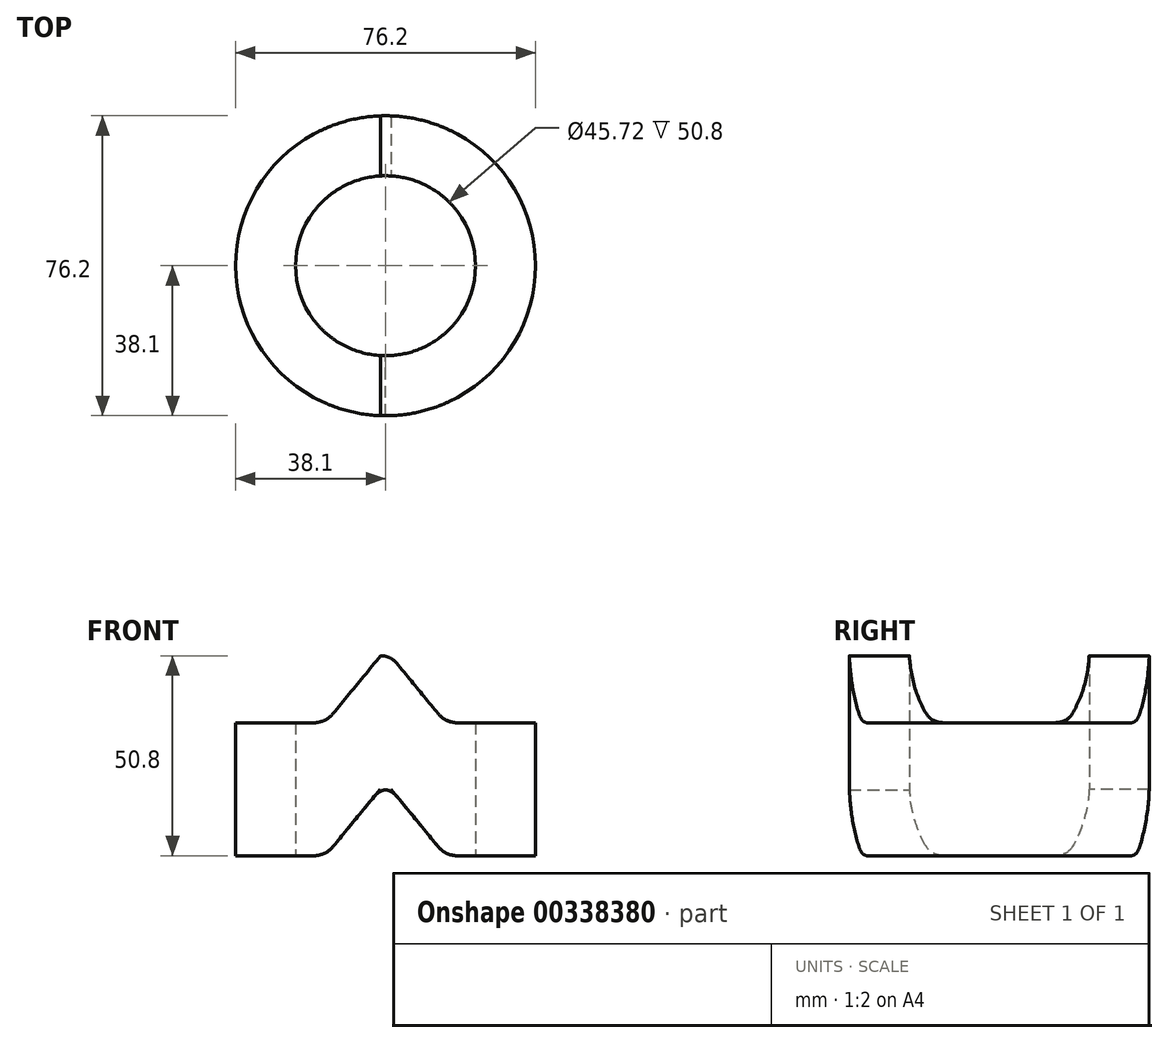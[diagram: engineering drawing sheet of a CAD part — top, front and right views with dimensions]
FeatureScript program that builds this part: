
annotation { "Feature Type Name" : "Feature", "Feature Type Description" : "" }
export const myFeature = defineFeature(function(context is Context, id is Id, definition is map)
    precondition{}
    {
        {
            var Q0;
            Q0=qCreatedBy(makeId("Top.planeOp"),FACE);
            var sketch = newSketch(context, id + "F0", { "sketchPlane" : qUnion([Q0])});
            skCircle(sketch, "E0", {"center": v(0, 0) * mm, "radius": 38.1 * mm});
            skCircle(sketch, "E1", {"center": v(0, 0) * mm, "radius": 22.86 * mm});
            skSolve(sketch);
        }
        {
            var Q0;
            Q0=makeQuery(id+"F0.imprint","IMPRINT",FACE,{"disambiguationData":[TD([[makeQuery(id+"F0.imprint","IMPRINT",EDGE,{"derivedFrom":sQuery(id+"F0.wireOp",EDGE,"E0")}),1.0]])]});
            extrude(context, id + "F1", {"entities" : qUnion([Q0]), "depth" : 127 * mm});
        }
        {
            var Q0;
            Q0=qCreatedBy(makeId("Front.planeOp"),FACE);
            cPlane(context, id + "F2", {"entities" : qUnion([Q0]), "cplaneType" : CPlaneType.OFFSET, "offset" : 41.9 * mm, "width" : 152.4 * mm, "height" : 152.4 * mm});
        }
        {
            var Q0;
            Q0=qCreatedBy(id+"F2.planeOp",FACE);
            var sketch = newSketch(context, id + "F3", { "sketchPlane" : qUnion([Q0])});
            skLineSegment(sketch, "E2.top", {"start": v(-38.1, 60.96) * mm, "end": v(-18.24, 60.96) * mm});
            skLineSegment(sketch, "E2.left", {"start": v(-38.1, 44.07) * mm, "end": v(-38.1, 60.96) * mm});
            skLineSegment(sketch, "E2.right", {"start": v(38.1, 44.07) * mm, "end": v(38.1, 60.96) * mm});
            skPoint(sketch, "E2.middle", {"position": v(0, 27.18) * mm});
            skPoint(sketch, "E2.bottom.start.orphan", {"position": v(-38.1, -6.6) * mm});
            skPoint(sketch, "E3.orphan", {"position": v(38.1, -6.6) * mm});
            skLineSegment(sketch, "E4", {"start": v(0, 77.98) * mm, "end": v(0, 27.18) * mm});
            skLineSegment(sketch, "E5", {"start": v(-1.24, 77.98) * mm, "end": v(1.24, 77.98) * mm});
            skLineSegment(sketch, "E6", {"start": v(1.29, 77.95) * mm, "end": v(13.33, 63.28) * mm});
            skLineSegment(sketch, "E7", {"start": v(-1.29, 77.95) * mm, "end": v(-13.33, 63.28) * mm});
            skPoint(sketch, "E8.newPointA", {"position": v(-15.24, 60.96) * mm});
            skPoint(sketch, "E8.newPointB", {"position": v(38.1, 60.96) * mm});
            skArc(sketch, "E8.filletArc", {"start": v(-18.24, 60.96) * mm, "mid": v(-15.53, 61.57) * mm, "end": v(-13.33, 63.28) * mm});
            skLineSegment(sketch, "E9", {"start": v(38.1, 60.96) * mm, "end": v(18.24, 60.96) * mm});
            skPoint(sketch, "E10.visualSharp", {"position": v(15.24, 60.96) * mm});
            skArc(sketch, "E10.filletArc", {"start": v(13.33, 63.28) * mm, "mid": v(15.53, 61.57) * mm, "end": v(18.24, 60.96) * mm});
            skPoint(sketch, "E11.visualSharp", {"position": v(1.27, 77.98) * mm});
            skPoint(sketch, "E12.visualSharp", {"position": v(-1.27, 77.98) * mm});
            skLineSegment(sketch, "E13", {"start": v(-38.1, 60.96) * mm, "end": v(-38.1, 77.98) * mm});
            skLineSegment(sketch, "E14", {"start": v(38.1, 60.96) * mm, "end": v(38.1, 80.6) * mm});
            skLineSegment(sketch, "E15", {"start": v(-0.13, 77.98) * mm, "end": v(-38.1, 77.98) * mm});
            skLineSegment(sketch, "E16", {"start": v(-38.1, 77.98) * mm, "end": v(38.1, 77.98) * mm});
            skLineSegment(sketch, "E17", {"start": v(-1.29, 77.95) * mm, "end": v(-1.27, 77.98) * mm});
            skLineSegment(sketch, "E18", {"start": v(1.29, 77.95) * mm, "end": v(1.27, 77.98) * mm});
            skLineSegment(sketch, "E19", {"start": v(-38.1, 44.07) * mm, "end": v(38.1, 44.07) * mm});
            skPoint(sketch, "E20.orphan", {"position": v(-38.1, 27.18) * mm});
            skPoint(sketch, "E21.orphan", {"position": v(38.1, 27.18) * mm});
            skLineSegment(sketch, "E22.top", {"start": v(-38.1, 27.18) * mm, "end": v(-18.24, 27.18) * mm});
            skLineSegment(sketch, "E22.left", {"start": v(-38.1, -6.6) * mm, "end": v(-38.1, 27.18) * mm});
            skLineSegment(sketch, "E22.right", {"start": v(38.1, -6.6) * mm, "end": v(38.1, 27.18) * mm});
            skPoint(sketch, "E22.middle", {"position": v(0, -6.6) * mm});
            skLineSegment(sketch, "E23", {"start": v(-38.1, -6.6) * mm, "end": v(38.1, -6.6) * mm});
            skPoint(sketch, "E22.bottom.start.orphan", {"position": v(-38.1, -40.39) * mm});
            skPoint(sketch, "E24.orphan", {"position": v(38.1, -40.39) * mm});
            skLineSegment(sketch, "E25", {"start": v(0, 44.2) * mm, "end": v(0, -6.6) * mm});
            skLineSegment(sketch, "E26", {"start": v(-1.24, 44.2) * mm, "end": v(1.24, 44.2) * mm});
            skLineSegment(sketch, "E27", {"start": v(1.29, 44.17) * mm, "end": v(13.33, 29.5) * mm});
            skLineSegment(sketch, "E28", {"start": v(-1.29, 44.17) * mm, "end": v(-13.33, 29.5) * mm});
            skPoint(sketch, "E29.newPointA", {"position": v(-15.24, 27.18) * mm});
            skArc(sketch, "E29.filletArc", {"start": v(-18.24, 27.18) * mm, "mid": v(-15.53, 27.79) * mm, "end": v(-13.33, 29.5) * mm});
            skLineSegment(sketch, "E30", {"start": v(38.1, 27.18) * mm, "end": v(18.24, 27.18) * mm});
            skPoint(sketch, "E31.visualSharp", {"position": v(15.24, 27.18) * mm});
            skArc(sketch, "E31.filletArc", {"start": v(13.33, 29.5) * mm, "mid": v(15.53, 27.79) * mm, "end": v(18.24, 27.18) * mm});
            skPoint(sketch, "E32.visualSharp", {"position": v(1.27, 44.2) * mm});
            skPoint(sketch, "E33.visualSharp", {"position": v(-1.27, 44.2) * mm});
            skLineSegment(sketch, "E34", {"start": v(-38.1, 27.18) * mm, "end": v(-38.1, 44.49) * mm});
            skLineSegment(sketch, "E35", {"start": v(38.1, 27.18) * mm, "end": v(38.1, 46.82) * mm});
            skLineSegment(sketch, "E36", {"start": v(-0.13, 44.2) * mm, "end": v(-38.1, 44.2) * mm});
            skLineSegment(sketch, "E37", {"start": v(-38.1, 44.2) * mm, "end": v(38.1, 44.2) * mm});
            skLineSegment(sketch, "E38", {"start": v(-1.29, 44.17) * mm, "end": v(-1.27, 44.2) * mm});
            skLineSegment(sketch, "E39", {"start": v(1.29, 44.17) * mm, "end": v(1.27, 44.2) * mm});
            skLineSegment(sketch, "E40", {"start": v(-38.1, 60.96) * mm, "end": v(-38.1, 27.18) * mm});
            skLineSegment(sketch, "E41", {"start": v(38.1, 27.18) * mm, "end": v(38.1, 60.96) * mm});
            skLineSegment(sketch, "E42.top", {"start": v(-38.1, 131.3) * mm, "end": v(38.1, 131.3) * mm});
            skLineSegment(sketch, "E42.left", {"start": v(-38.1, 77.98) * mm, "end": v(-38.1, 131.3) * mm});
            skLineSegment(sketch, "E42.right", {"start": v(38.1, 77.98) * mm, "end": v(38.1, 131.3) * mm});
            skSolve(sketch);
        }
        {
            var Q0;
            {var subQ5=sQuery(id+"F3.wireOp",EDGE,"E22.right");Q0=makeQuery(id+"F3.imprint","IMPRINT",FACE,{"disambiguationData":[TD([[makeQuery(id+"F3.imprint","IMPRINT",EDGE,{"derivedFrom":subQ5}),1.0]])]});}
            var Q1;
            Q1=makeQuery(id+"F3.imprint","IMPRINT",FACE,{"disambiguationData":[TD([[makeQuery(id+"F3.imprint","IMPRINT",EDGE,{"derivedFrom":sQuery(id+"F3.wireOp",EDGE,"E22.top")}),-1.0]])]});
            var Q2;
            Q2=makeQuery(id+"F3.imprint","IMPRINT",FACE,{"disambiguationData":[TD([[makeQuery(id+"F3.imprint","IMPRINT",EDGE,{"derivedFrom":sQuery(id+"F3.wireOp",EDGE,"E6")}),1.0]])]});
            var Q3;
            {var subQ1=sQuery(id+"F3.wireOp",EDGE,"E2.top");Q3=makeQuery(id+"F3.imprint","IMPRINT",FACE,{"disambiguationData":[TD([[makeQuery(id+"F3.imprint","IMPRINT",EDGE,{"derivedFrom":subQ1}),1.0]])]});}
            var Q4;
            {var subQ0=sQuery(id+"F3.wireOp",EDGE,"E16");Q4=makeQuery(id+"F3.imprint","IMPRINT",FACE,{"disambiguationData":[TD([[makeQuery(id+"F3.imprint","IMPRINT",EDGE,{"derivedFrom":subQ0}),1.0]])]});}
            extrude(context, id + "F4", {"entities" : qUnion([Q0, Q1, Q2, Q3, Q4]), "operationType" : NewBodyOperationType.REMOVE, "endBound" : BoundingType.THROUGH_ALL, "oppositeDirection" : true, "depth" : 25.4 * mm});
        }
        {
            var Q0;
            Q0=makeQuery(id+"F4.boolean.opBoolean","COPY",EDGE,{"disambiguationData":[OD(0.0)],"derivedFrom":makeQuery(id+"F4.opExtrude","SWEPT_EDGE",EDGE,{"disambiguationData":[OSD([sQuery(id+"F3.wireOp",EDGE,"E18"),sQuery(id+"F3.wireOp",EDGE,"E16")])]})});
            var Q1;
            Q1=makeQuery(id+"F4.boolean.opBoolean","COPY",EDGE,{"disambiguationData":[OD(0.0)],"derivedFrom":makeQuery(id+"F4.opExtrude","SWEPT_EDGE",EDGE,{"disambiguationData":[OSD([sQuery(id+"F3.wireOp",EDGE,"E17"),sQuery(id+"F3.wireOp",EDGE,"E16")])]})});
            var Q2;
            Q2=makeQuery(id+"F4.boolean.opBoolean","COPY",EDGE,{"disambiguationData":[OD(1.0)],"derivedFrom":makeQuery(id+"F4.opExtrude","SWEPT_EDGE",EDGE,{"disambiguationData":[OSD([sQuery(id+"F3.wireOp",EDGE,"E17"),sQuery(id+"F3.wireOp",EDGE,"E16")])]})});
            var Q3;
            Q3=makeQuery(id+"F4.boolean.opBoolean","COPY",EDGE,{"disambiguationData":[OD(1.0)],"derivedFrom":makeQuery(id+"F4.opExtrude","SWEPT_EDGE",EDGE,{"disambiguationData":[OSD([sQuery(id+"F3.wireOp",EDGE,"E18"),sQuery(id+"F3.wireOp",EDGE,"E16")])]})});
            var Q4;
            Q4=makeQuery(id+"F4.boolean.opBoolean","COPY",EDGE,{"disambiguationData":[OD(0.0)],"derivedFrom":makeQuery(id+"F4.opExtrude","SWEPT_EDGE",EDGE,{"disambiguationData":[OSD([sQuery(id+"F3.wireOp",EDGE,"E19"),sQuery(id+"F3.wireOp",EDGE,"E27")])]})});
            var Q5;
            Q5=makeQuery(id+"F4.boolean.opBoolean","COPY",EDGE,{"disambiguationData":[OD(0.0)],"derivedFrom":makeQuery(id+"F4.opExtrude","SWEPT_EDGE",EDGE,{"disambiguationData":[OSD([sQuery(id+"F3.wireOp",EDGE,"E19"),sQuery(id+"F3.wireOp",EDGE,"E28")])]})});
            fillet(context, id + "F5", {"entities" : qUnion([Q0, Q1, Q2, Q3, Q4, Q5]), "radius" : 5.08 * mm, "tangentPropagation" : true, "allowEdgeOverflow" : false});
        }
    });
